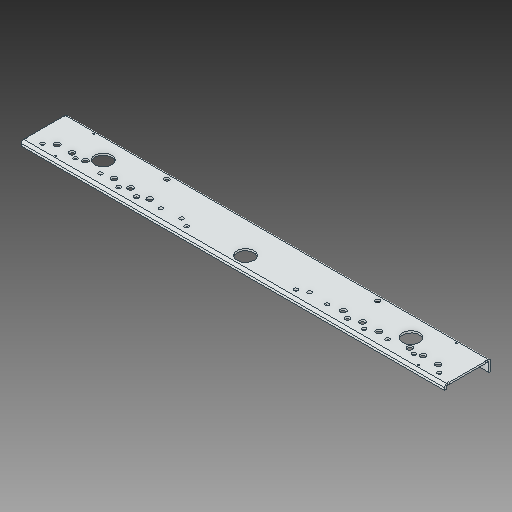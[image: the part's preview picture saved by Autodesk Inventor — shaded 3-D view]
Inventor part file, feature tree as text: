
AUTODESK INVENTOR PART (.ipt)
format: ipt  version: 2017 (Build 210142000, 142)  size: 223,744 bytes
history: native  units: in
note: dims shown in document units (in); Inventor stores cm internally (conversion verified against a paired STEP export)
features: other x4, reference x2, extrude x1, sketch x1
ambient origin geometry x8: Origin, YZ Plane, XZ Plane, XY Plane, X Axis, Y Axis, Z Axis, Center Point
bodies: Solid1 (feature_tree)
feature tree (8):
  extrude  "Extrusion1"  [1 undecoded]
  sketch  "Sketch1"  dims[d0=0.0in d1=0.0in]
  reference  "Reference1"
  reference  "Reference2"
  other  "Cut-Extrude10"
  other  "<userpath>\Documents\Inventor\2017 Robot\Robot Chassis.iam"
  other  "Robot Chassis.iam"
  other  "am-2952a_AM14U3_Inside_Plate:1"
note: 1 required parameter value undecoded (feature->parameter linkage not recoverable at this tier; creation-order binding heuristic only, values carry confidence <= 0.55)
